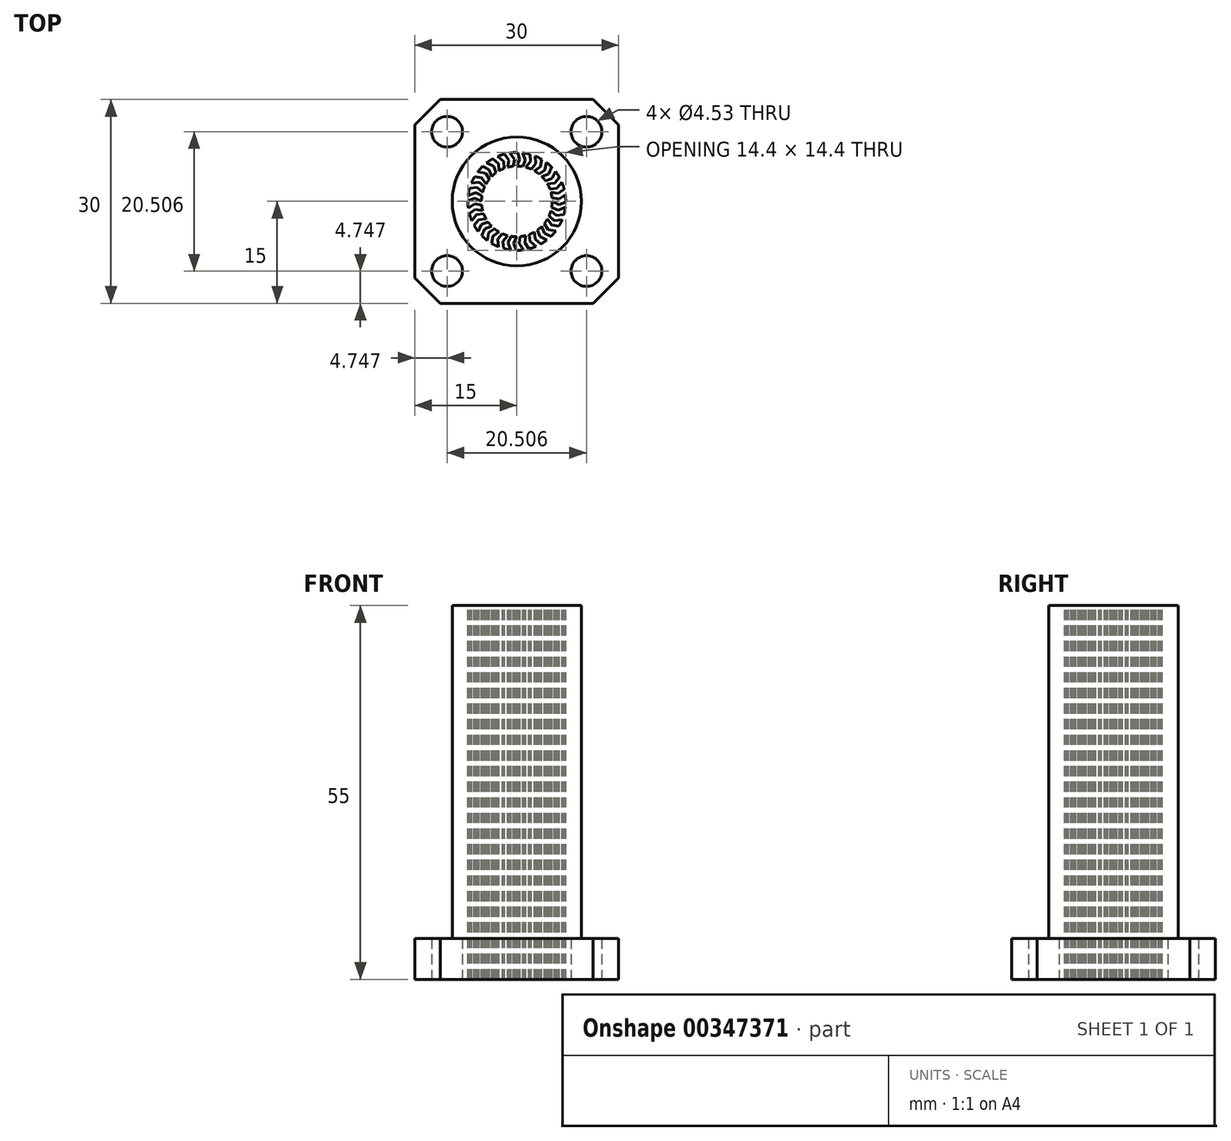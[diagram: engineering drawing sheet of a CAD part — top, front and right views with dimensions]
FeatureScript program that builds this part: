
annotation { "Feature Type Name" : "Feature", "Feature Type Description" : "" }
export const myFeature = defineFeature(function(context is Context, id is Id, definition is map)
    precondition{}
    {
        {
            var Q0;
            Q0=qCreatedBy(makeId("Top.planeOp"),FACE);
            var sketch = newSketch(context, id + "F0", { "sketchPlane" : qUnion([Q0])});
            skLineSegment(sketch, "E0.bottom", {"start": v(15, -15) * mm, "end": v(-15, -15) * mm});
            skLineSegment(sketch, "E0.top", {"start": v(15, 15) * mm, "end": v(-15, 15) * mm});
            skLineSegment(sketch, "E0.left", {"start": v(15, -15) * mm, "end": v(15, 15) * mm});
            skLineSegment(sketch, "E0.right", {"start": v(-15, -15) * mm, "end": v(-15, 15) * mm});
            skPoint(sketch, "E0.middle", {"position": v(0, 0) * mm});
            skSolve(sketch);
        }
        {
            var Q0;
            Q0=makeQuery(id+"F0.imprint","IMPRINT",FACE,{"disambiguationData":[TD([[makeQuery(id+"F0.imprint","IMPRINT",EDGE,{"derivedFrom":sQuery(id+"F0.wireOp",EDGE,"E0.bottom")}),-1.0]])]});
            extrude(context, id + "F1", {"entities" : qUnion([Q0]), "depth" : 6 * mm});
        }
        {
            var Q0;
            Q0=makeQuery(id+"F1.opExtrude","SWEPT_EDGE",EDGE,{"disambiguationData":[OSD([sQuery(id+"F0.wireOp",EDGE,"E0.bottom"),sQuery(id+"F0.wireOp",EDGE,"E0.right")])]});
            var Q1;
            Q1=makeQuery(id+"F1.opExtrude","SWEPT_EDGE",EDGE,{"disambiguationData":[OSD([sQuery(id+"F0.wireOp",EDGE,"E0.top"),sQuery(id+"F0.wireOp",EDGE,"E0.right")])]});
            var Q2;
            Q2=makeQuery(id+"F1.opExtrude","SWEPT_EDGE",EDGE,{"disambiguationData":[OSD([sQuery(id+"F0.wireOp",EDGE,"E0.bottom"),sQuery(id+"F0.wireOp",EDGE,"E0.left")])]});
            var Q3;
            Q3=makeQuery(id+"F1.opExtrude","SWEPT_EDGE",EDGE,{"disambiguationData":[OSD([sQuery(id+"F0.wireOp",EDGE,"E0.top"),sQuery(id+"F0.wireOp",EDGE,"E0.left")])]});
            chamfer(context, id + "F2", {"entities" : qUnion([Q0, Q1, Q2, Q3]), "width" : (7.5 / 2) * mm, "tangentPropagation" : true});
        }
        {
            var Q0;
            Q0=makeQuery(id+"F1.opExtrude","CAP_FACE",FACE,{"disambiguationData":[OSD([sQuery(id+"F0.wireOp",EDGE,"E0.bottom"),sQuery(id+"F0.wireOp",EDGE,"E0.top"),sQuery(id+"F0.wireOp",EDGE,"E0.left"),sQuery(id+"F0.wireOp",EDGE,"E0.right")])],"isStart":true});
            var sketch = newSketch(context, id + "F3", { "sketchPlane" : qUnion([Q0])});
            skCircle(sketch, "E1", {"center": v(0, 0) * mm, "radius": 14.5 * mm});
            skLineSegment(sketch, "E2", {"start": v(-13.13, 13.13) * mm, "end": v(13.13, -13.13) * mm});
            skLineSegment(sketch, "E3", {"start": v(-13.13, -13.12) * mm, "end": v(13.12, 13.12) * mm});
            skPoint(sketch, "E4", {"position": v(-10.25, 10.25) * mm});
            skPoint(sketch, "E5", {"position": v(10.25, 10.25) * mm});
            skPoint(sketch, "E6", {"position": v(10.25, -10.25) * mm});
            skPoint(sketch, "E7", {"position": v(-10.25, -10.25) * mm});
            skSolve(sketch);
        }
        {
            var Q0;
            Q0=sQuery(id+"F3.wireOp",VERTEX,"E4");
            var Q1;
            Q1=sQuery(id+"F3.wireOp",VERTEX,"E5");
            var Q2;
            Q2=sQuery(id+"F3.wireOp",VERTEX,"E7");
            var Q3;
            Q3=sQuery(id+"F3.wireOp",VERTEX,"E6");
            var Q4;
            Q4=makeQuery(id+"F1.opExtrude","SWEPT_BODY",BODY,{"disambiguationData":[OSD([sQuery(id+"F0.wireOp",EDGE,"E0.bottom"),sQuery(id+"F0.wireOp",EDGE,"E0.top"),sQuery(id+"F0.wireOp",EDGE,"E0.left"),sQuery(id+"F0.wireOp",EDGE,"E0.right")])]});
            hole(context, id + "F4", {"style" : HoleStyle.SIMPLE, "endStyle" : HoleEndStyle.THROUGH, "holeDiameter" : 4.53 * mm, "isTappedThrough" : true, "tappedDepth" : 12 * mm, "tapClearance" : 3, "locations" : qUnion([Q0, Q1, Q2, Q3]), "scope" : qUnion([Q4])});
        }
        {
            var Q0;
            Q0=makeQuery(id+"F1.opExtrude","CAP_FACE",FACE,{"disambiguationData":[OSD([sQuery(id+"F0.wireOp",EDGE,"E0.bottom"),sQuery(id+"F0.wireOp",EDGE,"E0.top"),sQuery(id+"F0.wireOp",EDGE,"E0.left"),sQuery(id+"F0.wireOp",EDGE,"E0.right")])],"isStart":false});
            var sketch = newSketch(context, id + "F5", { "sketchPlane" : qUnion([Q0])});
            skCircle(sketch, "E8", {"center": v(0, 0) * mm, "radius": 9.5 * mm});
            skSolve(sketch);
        }
        {
            var Q0;
            Q0=makeQuery(id+"F5.imprint","IMPRINT",FACE,{"disambiguationData":[TD([[makeQuery(id+"F5.imprint","IMPRINT",EDGE,{"derivedFrom":sQuery(id+"F5.wireOp",EDGE,"E8")}),1.0]])]});
            extrude(context, id + "F6", {"entities" : qUnion([Q0]), "operationType" : NewBodyOperationType.ADD, "depth" : 49 * mm});
        }
        {
            var Q0;
            Q0=makeQuery(id+"F6.opExtrude","CAP_FACE",FACE,{"disambiguationData":[OSD([sQuery(id+"F5.wireOp",EDGE,"E8")])],"isStart":false});
            var sketch = newSketch(context, id + "F7", { "sketchPlane" : qUnion([Q0])});
            skCircle(sketch, "E9", {"center": v(0, 0) * mm, "radius": 5.2 * mm});
            skSolve(sketch);
        }
        {
            var Q0;
            Q0=makeQuery(id+"F7.imprint","IMPRINT",FACE,{"disambiguationData":[TD([[makeQuery(id+"F7.imprint","IMPRINT",EDGE,{"derivedFrom":sQuery(id+"F7.wireOp",EDGE,"E9")}),1.0]])]});
            extrude(context, id + "F8", {"entities" : qUnion([Q0]), "operationType" : NewBodyOperationType.REMOVE, "endBound" : BoundingType.UP_TO_NEXT, "oppositeDirection" : true, "depth" : 25 * mm});
        }
        {
            var Q0;
            Q0=makeQuery(id+"F6.opExtrude","CAP_FACE",FACE,{"disambiguationData":[OSD([sQuery(id+"F5.wireOp",EDGE,"E8")])],"isStart":false});
            var sketch = newSketch(context, id + "F9", { "sketchPlane" : qUnion([Q0])});
            skCircle(sketch, "E10.cCircle", {"center": v(0, 5.2) * mm, "radius": 0.5 * mm, "construction": true});
            skLineSegment(sketch, "E10.0", {"start": v(0.29, 4.7) * mm, "end": v(-0.29, 4.7) * mm});
            skLineSegment(sketch, "E10.1", {"start": v(-0.29, 4.7) * mm, "end": v(-0.58, 5.2) * mm});
            skLineSegment(sketch, "E10.2", {"start": v(-0.58, 5.2) * mm, "end": v(-0.29, 5.7) * mm});
            skLineSegment(sketch, "E10.3", {"start": v(-0.29, 5.7) * mm, "end": v(0.29, 5.7) * mm});
            skLineSegment(sketch, "E10.4", {"start": v(0.29, 5.7) * mm, "end": v(0.58, 5.2) * mm});
            skLineSegment(sketch, "E10.5", {"start": v(0.58, 5.2) * mm, "end": v(0.29, 4.7) * mm});
            skPoint(sketch, "E10.0.midPoint", {"position": v(0, 4.7) * mm});
            skLineSegment(sketch, "E11.1.0", {"start": v(-1.91, 5.38) * mm, "end": v(-1.46, 5.03) * mm});
            skPoint(sketch, "E11.1.1", {"position": v(-1.8, 4.34) * mm});
            skCircle(sketch, "E11.1.2", {"center": v(-1.99, 4.8) * mm, "radius": 0.5 * mm, "construction": true});
            skLineSegment(sketch, "E11.1.3", {"start": v(-1.53, 4.45) * mm, "end": v(-2.07, 4.23) * mm});
            skLineSegment(sketch, "E11.1.4", {"start": v(-2.07, 4.23) * mm, "end": v(-2.52, 4.58) * mm});
            skLineSegment(sketch, "E11.1.5", {"start": v(-2.52, 4.58) * mm, "end": v(-2.45, 5.16) * mm});
            skLineSegment(sketch, "E11.1.6", {"start": v(-2.45, 5.16) * mm, "end": v(-1.91, 5.38) * mm});
            skLineSegment(sketch, "E11.1.7", {"start": v(-1.46, 5.03) * mm, "end": v(-1.53, 4.45) * mm});
            skLineSegment(sketch, "E11.2.0", {"start": v(-3.83, 4.23) * mm, "end": v(-3.27, 4.09) * mm});
            skPoint(sketch, "E11.2.1", {"position": v(-3.32, 3.32) * mm});
            skCircle(sketch, "E11.2.2", {"center": v(-3.68, 3.68) * mm, "radius": 0.5 * mm, "construction": true});
            skLineSegment(sketch, "E11.2.3", {"start": v(-3.12, 3.53) * mm, "end": v(-3.53, 3.12) * mm});
            skLineSegment(sketch, "E11.2.4", {"start": v(-3.53, 3.12) * mm, "end": v(-4.09, 3.27) * mm});
            skLineSegment(sketch, "E11.2.5", {"start": v(-4.09, 3.27) * mm, "end": v(-4.23, 3.83) * mm});
            skLineSegment(sketch, "E11.2.6", {"start": v(-4.23, 3.83) * mm, "end": v(-3.83, 4.23) * mm});
            skLineSegment(sketch, "E11.2.7", {"start": v(-3.27, 4.09) * mm, "end": v(-3.12, 3.53) * mm});
            skLineSegment(sketch, "E11.3.0", {"start": v(-5.16, 2.45) * mm, "end": v(-4.58, 2.52) * mm});
            skPoint(sketch, "E11.3.1", {"position": v(-4.34, 1.8) * mm});
            skCircle(sketch, "E11.3.2", {"center": v(-4.8, 1.99) * mm, "radius": 0.5 * mm, "construction": true});
            skLineSegment(sketch, "E11.3.3", {"start": v(-4.23, 2.07) * mm, "end": v(-4.45, 1.53) * mm});
            skLineSegment(sketch, "E11.3.4", {"start": v(-4.45, 1.53) * mm, "end": v(-5.03, 1.46) * mm});
            skLineSegment(sketch, "E11.3.5", {"start": v(-5.03, 1.46) * mm, "end": v(-5.38, 1.91) * mm});
            skLineSegment(sketch, "E11.3.6", {"start": v(-5.38, 1.91) * mm, "end": v(-5.16, 2.45) * mm});
            skLineSegment(sketch, "E11.3.7", {"start": v(-4.58, 2.52) * mm, "end": v(-4.23, 2.07) * mm});
            skLineSegment(sketch, "E11.4.0", {"start": v(-5.7, 0.29) * mm, "end": v(-5.2, 0.58) * mm});
            skPoint(sketch, "E11.4.1", {"position": v(-4.7, 0) * mm});
            skCircle(sketch, "E11.4.2", {"center": v(-5.2, 0) * mm, "radius": 0.5 * mm, "construction": true});
            skLineSegment(sketch, "E11.4.3", {"start": v(-4.7, 0.29) * mm, "end": v(-4.7, -0.29) * mm});
            skLineSegment(sketch, "E11.4.4", {"start": v(-4.7, -0.29) * mm, "end": v(-5.2, -0.58) * mm});
            skLineSegment(sketch, "E11.4.5", {"start": v(-5.2, -0.58) * mm, "end": v(-5.7, -0.29) * mm});
            skLineSegment(sketch, "E11.4.6", {"start": v(-5.7, -0.29) * mm, "end": v(-5.7, 0.29) * mm});
            skLineSegment(sketch, "E11.4.7", {"start": v(-5.2, 0.58) * mm, "end": v(-4.7, 0.29) * mm});
            skLineSegment(sketch, "E11.5.0", {"start": v(-5.38, -1.91) * mm, "end": v(-5.03, -1.46) * mm});
            skPoint(sketch, "E11.5.1", {"position": v(-4.34, -1.8) * mm});
            skCircle(sketch, "E11.5.2", {"center": v(-4.8, -1.99) * mm, "radius": 0.5 * mm, "construction": true});
            skLineSegment(sketch, "E11.5.3", {"start": v(-4.45, -1.53) * mm, "end": v(-4.23, -2.07) * mm});
            skLineSegment(sketch, "E11.5.4", {"start": v(-4.23, -2.07) * mm, "end": v(-4.58, -2.52) * mm});
            skLineSegment(sketch, "E11.5.5", {"start": v(-4.58, -2.52) * mm, "end": v(-5.16, -2.45) * mm});
            skLineSegment(sketch, "E11.5.6", {"start": v(-5.16, -2.45) * mm, "end": v(-5.38, -1.91) * mm});
            skLineSegment(sketch, "E11.5.7", {"start": v(-5.03, -1.46) * mm, "end": v(-4.45, -1.53) * mm});
            skLineSegment(sketch, "E11.6.0", {"start": v(-4.23, -3.83) * mm, "end": v(-4.09, -3.27) * mm});
            skPoint(sketch, "E11.6.1", {"position": v(-3.32, -3.32) * mm});
            skCircle(sketch, "E11.6.2", {"center": v(-3.68, -3.68) * mm, "radius": 0.5 * mm, "construction": true});
            skLineSegment(sketch, "E11.6.3", {"start": v(-3.53, -3.12) * mm, "end": v(-3.12, -3.53) * mm});
            skLineSegment(sketch, "E11.6.4", {"start": v(-3.12, -3.53) * mm, "end": v(-3.27, -4.09) * mm});
            skLineSegment(sketch, "E11.6.5", {"start": v(-3.27, -4.09) * mm, "end": v(-3.83, -4.23) * mm});
            skLineSegment(sketch, "E11.6.6", {"start": v(-3.83, -4.23) * mm, "end": v(-4.23, -3.83) * mm});
            skLineSegment(sketch, "E11.6.7", {"start": v(-4.09, -3.27) * mm, "end": v(-3.53, -3.12) * mm});
            skLineSegment(sketch, "E11.7.0", {"start": v(-2.45, -5.16) * mm, "end": v(-2.52, -4.58) * mm});
            skPoint(sketch, "E11.7.1", {"position": v(-1.8, -4.34) * mm});
            skCircle(sketch, "E11.7.2", {"center": v(-1.99, -4.8) * mm, "radius": 0.5 * mm, "construction": true});
            skLineSegment(sketch, "E11.7.3", {"start": v(-2.07, -4.23) * mm, "end": v(-1.53, -4.45) * mm});
            skLineSegment(sketch, "E11.7.4", {"start": v(-1.53, -4.45) * mm, "end": v(-1.46, -5.03) * mm});
            skLineSegment(sketch, "E11.7.5", {"start": v(-1.46, -5.03) * mm, "end": v(-1.91, -5.38) * mm});
            skLineSegment(sketch, "E11.7.6", {"start": v(-1.91, -5.38) * mm, "end": v(-2.45, -5.16) * mm});
            skLineSegment(sketch, "E11.7.7", {"start": v(-2.52, -4.58) * mm, "end": v(-2.07, -4.23) * mm});
            skLineSegment(sketch, "E11.8.0", {"start": v(-0.29, -5.7) * mm, "end": v(-0.58, -5.2) * mm});
            skPoint(sketch, "E11.8.1", {"position": v(0, -4.7) * mm});
            skCircle(sketch, "E11.8.2", {"center": v(0, -5.2) * mm, "radius": 0.5 * mm, "construction": true});
            skLineSegment(sketch, "E11.8.3", {"start": v(-0.29, -4.7) * mm, "end": v(0.29, -4.7) * mm});
            skLineSegment(sketch, "E11.8.4", {"start": v(0.29, -4.7) * mm, "end": v(0.58, -5.2) * mm});
            skLineSegment(sketch, "E11.8.5", {"start": v(0.58, -5.2) * mm, "end": v(0.29, -5.7) * mm});
            skLineSegment(sketch, "E11.8.6", {"start": v(0.29, -5.7) * mm, "end": v(-0.29, -5.7) * mm});
            skLineSegment(sketch, "E11.8.7", {"start": v(-0.58, -5.2) * mm, "end": v(-0.29, -4.7) * mm});
            skLineSegment(sketch, "E11.9.0", {"start": v(1.91, -5.38) * mm, "end": v(1.46, -5.03) * mm});
            skPoint(sketch, "E11.9.1", {"position": v(1.8, -4.34) * mm});
            skCircle(sketch, "E11.9.2", {"center": v(1.99, -4.8) * mm, "radius": 0.5 * mm, "construction": true});
            skLineSegment(sketch, "E11.9.3", {"start": v(1.53, -4.45) * mm, "end": v(2.07, -4.23) * mm});
            skLineSegment(sketch, "E11.9.4", {"start": v(2.07, -4.23) * mm, "end": v(2.52, -4.58) * mm});
            skLineSegment(sketch, "E11.9.5", {"start": v(2.52, -4.58) * mm, "end": v(2.45, -5.16) * mm});
            skLineSegment(sketch, "E11.9.6", {"start": v(2.45, -5.16) * mm, "end": v(1.91, -5.38) * mm});
            skLineSegment(sketch, "E11.9.7", {"start": v(1.46, -5.03) * mm, "end": v(1.53, -4.45) * mm});
            skLineSegment(sketch, "E11.10.0", {"start": v(3.83, -4.23) * mm, "end": v(3.27, -4.09) * mm});
            skPoint(sketch, "E11.10.1", {"position": v(3.32, -3.32) * mm});
            skCircle(sketch, "E11.10.2", {"center": v(3.68, -3.68) * mm, "radius": 0.5 * mm, "construction": true});
            skLineSegment(sketch, "E11.10.3", {"start": v(3.12, -3.53) * mm, "end": v(3.53, -3.12) * mm});
            skLineSegment(sketch, "E11.10.4", {"start": v(3.53, -3.12) * mm, "end": v(4.09, -3.27) * mm});
            skLineSegment(sketch, "E11.10.5", {"start": v(4.09, -3.27) * mm, "end": v(4.23, -3.83) * mm});
            skLineSegment(sketch, "E11.10.6", {"start": v(4.23, -3.83) * mm, "end": v(3.83, -4.23) * mm});
            skLineSegment(sketch, "E11.10.7", {"start": v(3.27, -4.09) * mm, "end": v(3.12, -3.53) * mm});
            skLineSegment(sketch, "E11.11.0", {"start": v(5.16, -2.45) * mm, "end": v(4.58, -2.52) * mm});
            skPoint(sketch, "E11.11.1", {"position": v(4.34, -1.8) * mm});
            skCircle(sketch, "E11.11.2", {"center": v(4.8, -1.99) * mm, "radius": 0.5 * mm, "construction": true});
            skLineSegment(sketch, "E11.11.3", {"start": v(4.23, -2.07) * mm, "end": v(4.45, -1.53) * mm});
            skLineSegment(sketch, "E11.11.4", {"start": v(4.45, -1.53) * mm, "end": v(5.03, -1.46) * mm});
            skLineSegment(sketch, "E11.11.5", {"start": v(5.03, -1.46) * mm, "end": v(5.38, -1.91) * mm});
            skLineSegment(sketch, "E11.11.6", {"start": v(5.38, -1.91) * mm, "end": v(5.16, -2.45) * mm});
            skLineSegment(sketch, "E11.11.7", {"start": v(4.58, -2.52) * mm, "end": v(4.23, -2.07) * mm});
            skLineSegment(sketch, "E11.12.0", {"start": v(5.7, -0.29) * mm, "end": v(5.2, -0.58) * mm});
            skPoint(sketch, "E11.12.1", {"position": v(4.7, 0) * mm});
            skCircle(sketch, "E11.12.2", {"center": v(5.2, 0) * mm, "radius": 0.5 * mm, "construction": true});
            skLineSegment(sketch, "E11.12.3", {"start": v(4.7, -0.29) * mm, "end": v(4.7, 0.29) * mm});
            skLineSegment(sketch, "E11.12.4", {"start": v(4.7, 0.29) * mm, "end": v(5.2, 0.58) * mm});
            skLineSegment(sketch, "E11.12.5", {"start": v(5.2, 0.58) * mm, "end": v(5.7, 0.29) * mm});
            skLineSegment(sketch, "E11.12.6", {"start": v(5.7, 0.29) * mm, "end": v(5.7, -0.29) * mm});
            skLineSegment(sketch, "E11.12.7", {"start": v(5.2, -0.58) * mm, "end": v(4.7, -0.29) * mm});
            skLineSegment(sketch, "E11.13.0", {"start": v(5.38, 1.91) * mm, "end": v(5.03, 1.46) * mm});
            skPoint(sketch, "E11.13.1", {"position": v(4.34, 1.8) * mm});
            skCircle(sketch, "E11.13.2", {"center": v(4.8, 1.99) * mm, "radius": 0.5 * mm, "construction": true});
            skLineSegment(sketch, "E11.13.3", {"start": v(4.45, 1.53) * mm, "end": v(4.23, 2.07) * mm});
            skLineSegment(sketch, "E11.13.4", {"start": v(4.23, 2.07) * mm, "end": v(4.58, 2.52) * mm});
            skLineSegment(sketch, "E11.13.5", {"start": v(4.58, 2.52) * mm, "end": v(5.16, 2.45) * mm});
            skLineSegment(sketch, "E11.13.6", {"start": v(5.16, 2.45) * mm, "end": v(5.38, 1.91) * mm});
            skLineSegment(sketch, "E11.13.7", {"start": v(5.03, 1.46) * mm, "end": v(4.45, 1.53) * mm});
            skLineSegment(sketch, "E11.14.0", {"start": v(4.23, 3.83) * mm, "end": v(4.09, 3.27) * mm});
            skPoint(sketch, "E11.14.1", {"position": v(3.32, 3.32) * mm});
            skCircle(sketch, "E11.14.2", {"center": v(3.68, 3.68) * mm, "radius": 0.5 * mm, "construction": true});
            skLineSegment(sketch, "E11.14.3", {"start": v(3.53, 3.12) * mm, "end": v(3.12, 3.53) * mm});
            skLineSegment(sketch, "E11.14.4", {"start": v(3.12, 3.53) * mm, "end": v(3.27, 4.09) * mm});
            skLineSegment(sketch, "E11.14.5", {"start": v(3.27, 4.09) * mm, "end": v(3.83, 4.23) * mm});
            skLineSegment(sketch, "E11.14.6", {"start": v(3.83, 4.23) * mm, "end": v(4.23, 3.83) * mm});
            skLineSegment(sketch, "E11.14.7", {"start": v(4.09, 3.27) * mm, "end": v(3.53, 3.12) * mm});
            skLineSegment(sketch, "E11.15.0", {"start": v(2.45, 5.16) * mm, "end": v(2.52, 4.58) * mm});
            skPoint(sketch, "E11.15.1", {"position": v(1.8, 4.34) * mm});
            skCircle(sketch, "E11.15.2", {"center": v(1.99, 4.8) * mm, "radius": 0.5 * mm, "construction": true});
            skLineSegment(sketch, "E11.15.3", {"start": v(2.07, 4.23) * mm, "end": v(1.53, 4.45) * mm});
            skLineSegment(sketch, "E11.15.4", {"start": v(1.53, 4.45) * mm, "end": v(1.46, 5.03) * mm});
            skLineSegment(sketch, "E11.15.5", {"start": v(1.46, 5.03) * mm, "end": v(1.91, 5.38) * mm});
            skLineSegment(sketch, "E11.15.6", {"start": v(1.91, 5.38) * mm, "end": v(2.45, 5.16) * mm});
            skLineSegment(sketch, "E11.15.7", {"start": v(2.52, 4.58) * mm, "end": v(2.07, 4.23) * mm});
            skPoint(sketch, "E11.center", {"position": v(0, 0) * mm});
            skSolve(sketch);
        }
        {
            var Q0;
            Q0=makeQuery(id+"F6.opExtrude","CAP_FACE",FACE,{"disambiguationData":[OSD([sQuery(id+"F5.wireOp",EDGE,"E8")])],"isStart":false});
            var sketch = newSketch(context, id + "F10", { "sketchPlane" : qUnion([Q0])});
            skLineSegment(sketch, "E12.bottom", {"start": v(0.5, 3.7) * mm, "end": v(-0.5, 3.7) * mm});
            skLineSegment(sketch, "E12.top", {"start": v(0.5, 6.7) * mm, "end": v(-0.5, 6.7) * mm});
            skLineSegment(sketch, "E12.left", {"start": v(0.5, 3.7) * mm, "end": v(0.5, 6.7) * mm});
            skLineSegment(sketch, "E12.right", {"start": v(-0.5, 3.7) * mm, "end": v(-0.5, 6.7) * mm});
            skPoint(sketch, "E12.middle", {"position": v(0, 5.2) * mm});
            skLineSegment(sketch, "E13.1.0", {"start": v(-0.95, 3.6) * mm, "end": v(-2.1, 6.38) * mm});
            skLineSegment(sketch, "E13.1.1", {"start": v(-2.1, 6.38) * mm, "end": v(-3.03, 6) * mm});
            skLineSegment(sketch, "E13.1.2", {"start": v(-0.95, 3.6) * mm, "end": v(-1.88, 3.23) * mm});
            skPoint(sketch, "E13.1.3", {"position": v(-1.99, 4.8) * mm});
            skLineSegment(sketch, "E13.1.4", {"start": v(-1.88, 3.23) * mm, "end": v(-3.03, 6) * mm});
            skLineSegment(sketch, "E13.2.0", {"start": v(-2.26, 2.97) * mm, "end": v(-4.38, 5.1) * mm});
            skLineSegment(sketch, "E13.2.1", {"start": v(-4.38, 5.1) * mm, "end": v(-5.1, 4.38) * mm});
            skLineSegment(sketch, "E13.2.2", {"start": v(-2.26, 2.97) * mm, "end": v(-2.97, 2.26) * mm});
            skPoint(sketch, "E13.2.3", {"position": v(-3.68, 3.68) * mm});
            skLineSegment(sketch, "E13.2.4", {"start": v(-2.97, 2.26) * mm, "end": v(-5.1, 4.38) * mm});
            skLineSegment(sketch, "E13.3.0", {"start": v(-3.23, 1.88) * mm, "end": v(-6, 3.03) * mm});
            skLineSegment(sketch, "E13.3.1", {"start": v(-6, 3.03) * mm, "end": v(-6.38, 2.1) * mm});
            skLineSegment(sketch, "E13.3.2", {"start": v(-3.23, 1.88) * mm, "end": v(-3.6, 0.95) * mm});
            skPoint(sketch, "E13.3.3", {"position": v(-4.8, 1.99) * mm});
            skLineSegment(sketch, "E13.3.4", {"start": v(-3.6, 0.95) * mm, "end": v(-6.38, 2.1) * mm});
            skLineSegment(sketch, "E13.4.0", {"start": v(-3.7, 0.5) * mm, "end": v(-6.7, 0.5) * mm});
            skLineSegment(sketch, "E13.4.1", {"start": v(-6.7, 0.5) * mm, "end": v(-6.7, -0.5) * mm});
            skLineSegment(sketch, "E13.4.2", {"start": v(-3.7, 0.5) * mm, "end": v(-3.7, -0.5) * mm});
            skPoint(sketch, "E13.4.3", {"position": v(-5.2, 0) * mm});
            skLineSegment(sketch, "E13.4.4", {"start": v(-3.7, -0.5) * mm, "end": v(-6.7, -0.5) * mm});
            skLineSegment(sketch, "E13.5.0", {"start": v(-3.6, -0.95) * mm, "end": v(-6.38, -2.1) * mm});
            skLineSegment(sketch, "E13.5.1", {"start": v(-6.38, -2.1) * mm, "end": v(-6, -3.03) * mm});
            skLineSegment(sketch, "E13.5.2", {"start": v(-3.6, -0.95) * mm, "end": v(-3.23, -1.88) * mm});
            skPoint(sketch, "E13.5.3", {"position": v(-4.8, -1.99) * mm});
            skLineSegment(sketch, "E13.5.4", {"start": v(-3.23, -1.88) * mm, "end": v(-6, -3.03) * mm});
            skLineSegment(sketch, "E13.6.0", {"start": v(-2.97, -2.26) * mm, "end": v(-5.1, -4.38) * mm});
            skLineSegment(sketch, "E13.6.1", {"start": v(-5.1, -4.38) * mm, "end": v(-4.38, -5.1) * mm});
            skLineSegment(sketch, "E13.6.2", {"start": v(-2.97, -2.26) * mm, "end": v(-2.26, -2.97) * mm});
            skPoint(sketch, "E13.6.3", {"position": v(-3.68, -3.68) * mm});
            skLineSegment(sketch, "E13.6.4", {"start": v(-2.26, -2.97) * mm, "end": v(-4.38, -5.1) * mm});
            skLineSegment(sketch, "E13.7.0", {"start": v(-1.88, -3.23) * mm, "end": v(-3.03, -6) * mm});
            skLineSegment(sketch, "E13.7.1", {"start": v(-3.03, -6) * mm, "end": v(-2.1, -6.38) * mm});
            skLineSegment(sketch, "E13.7.2", {"start": v(-1.88, -3.23) * mm, "end": v(-0.95, -3.6) * mm});
            skPoint(sketch, "E13.7.3", {"position": v(-1.99, -4.8) * mm});
            skLineSegment(sketch, "E13.7.4", {"start": v(-0.95, -3.6) * mm, "end": v(-2.1, -6.38) * mm});
            skLineSegment(sketch, "E13.8.0", {"start": v(-0.5, -3.7) * mm, "end": v(-0.5, -6.7) * mm});
            skLineSegment(sketch, "E13.8.1", {"start": v(-0.5, -6.7) * mm, "end": v(0.5, -6.7) * mm});
            skLineSegment(sketch, "E13.8.2", {"start": v(-0.5, -3.7) * mm, "end": v(0.5, -3.7) * mm});
            skPoint(sketch, "E13.8.3", {"position": v(0, -5.2) * mm});
            skLineSegment(sketch, "E13.8.4", {"start": v(0.5, -3.7) * mm, "end": v(0.5, -6.7) * mm});
            skLineSegment(sketch, "E13.9.0", {"start": v(0.95, -3.6) * mm, "end": v(2.1, -6.38) * mm});
            skLineSegment(sketch, "E13.9.1", {"start": v(2.1, -6.38) * mm, "end": v(3.03, -6) * mm});
            skLineSegment(sketch, "E13.9.2", {"start": v(0.95, -3.6) * mm, "end": v(1.88, -3.23) * mm});
            skPoint(sketch, "E13.9.3", {"position": v(1.99, -4.8) * mm});
            skLineSegment(sketch, "E13.9.4", {"start": v(1.88, -3.23) * mm, "end": v(3.03, -6) * mm});
            skLineSegment(sketch, "E13.10.0", {"start": v(2.26, -2.97) * mm, "end": v(4.38, -5.1) * mm});
            skLineSegment(sketch, "E13.10.1", {"start": v(4.38, -5.1) * mm, "end": v(5.1, -4.38) * mm});
            skLineSegment(sketch, "E13.10.2", {"start": v(2.26, -2.97) * mm, "end": v(2.97, -2.26) * mm});
            skPoint(sketch, "E13.10.3", {"position": v(3.68, -3.68) * mm});
            skLineSegment(sketch, "E13.10.4", {"start": v(2.97, -2.26) * mm, "end": v(5.1, -4.38) * mm});
            skLineSegment(sketch, "E13.11.0", {"start": v(3.23, -1.88) * mm, "end": v(6, -3.03) * mm});
            skLineSegment(sketch, "E13.11.1", {"start": v(6, -3.03) * mm, "end": v(6.38, -2.1) * mm});
            skLineSegment(sketch, "E13.11.2", {"start": v(3.23, -1.88) * mm, "end": v(3.6, -0.95) * mm});
            skPoint(sketch, "E13.11.3", {"position": v(4.8, -1.99) * mm});
            skLineSegment(sketch, "E13.11.4", {"start": v(3.6, -0.95) * mm, "end": v(6.38, -2.1) * mm});
            skLineSegment(sketch, "E13.12.0", {"start": v(3.7, -0.5) * mm, "end": v(6.7, -0.5) * mm});
            skLineSegment(sketch, "E13.12.1", {"start": v(6.7, -0.5) * mm, "end": v(6.7, 0.5) * mm});
            skLineSegment(sketch, "E13.12.2", {"start": v(3.7, -0.5) * mm, "end": v(3.7, 0.5) * mm});
            skPoint(sketch, "E13.12.3", {"position": v(5.2, 0) * mm});
            skLineSegment(sketch, "E13.12.4", {"start": v(3.7, 0.5) * mm, "end": v(6.7, 0.5) * mm});
            skLineSegment(sketch, "E13.13.0", {"start": v(3.6, 0.95) * mm, "end": v(6.38, 2.1) * mm});
            skLineSegment(sketch, "E13.13.1", {"start": v(6.38, 2.1) * mm, "end": v(6, 3.03) * mm});
            skLineSegment(sketch, "E13.13.2", {"start": v(3.6, 0.95) * mm, "end": v(3.23, 1.88) * mm});
            skPoint(sketch, "E13.13.3", {"position": v(4.8, 1.99) * mm});
            skLineSegment(sketch, "E13.13.4", {"start": v(3.23, 1.88) * mm, "end": v(6, 3.03) * mm});
            skLineSegment(sketch, "E13.14.0", {"start": v(2.97, 2.26) * mm, "end": v(5.1, 4.38) * mm});
            skLineSegment(sketch, "E13.14.1", {"start": v(5.1, 4.38) * mm, "end": v(4.38, 5.1) * mm});
            skLineSegment(sketch, "E13.14.2", {"start": v(2.97, 2.26) * mm, "end": v(2.26, 2.97) * mm});
            skPoint(sketch, "E13.14.3", {"position": v(3.68, 3.68) * mm});
            skLineSegment(sketch, "E13.14.4", {"start": v(2.26, 2.97) * mm, "end": v(4.38, 5.1) * mm});
            skLineSegment(sketch, "E13.15.0", {"start": v(1.88, 3.23) * mm, "end": v(3.03, 6) * mm});
            skLineSegment(sketch, "E13.15.1", {"start": v(3.03, 6) * mm, "end": v(2.1, 6.38) * mm});
            skLineSegment(sketch, "E13.15.2", {"start": v(1.88, 3.23) * mm, "end": v(0.95, 3.6) * mm});
            skPoint(sketch, "E13.15.3", {"position": v(1.99, 4.8) * mm});
            skLineSegment(sketch, "E13.15.4", {"start": v(0.95, 3.6) * mm, "end": v(2.1, 6.38) * mm});
            skPoint(sketch, "E13.center", {"position": v(0, 0) * mm});
            skSolve(sketch);
        }
        {
            var Q0;
            Q0=makeQuery(id+"F6.opExtrude","CAP_FACE",FACE,{"disambiguationData":[OSD([sQuery(id+"F5.wireOp",EDGE,"E8")])],"isStart":false});
            var sketch = newSketch(context, id + "F11", { "sketchPlane" : qUnion([Q0])});
            skCircle(sketch, "E14", {"center": v(0, 0) * mm, "radius": 6.2 * mm});
            skCircle(sketch, "E15", {"center": v(0, 0) * mm, "radius": 7.2 * mm});
            skLineSegment(sketch, "E16", {"start": v(0, 5.2) * mm, "end": v(0.45, 6.18) * mm});
            skLineSegment(sketch, "E17", {"start": v(0.45, 6.18) * mm, "end": v(0.08, 7.2) * mm});
            skLineSegment(sketch, "E18", {"start": v(0.84, 5.13) * mm, "end": v(1.28, 6.07) * mm});
            skLineSegment(sketch, "E19", {"start": v(1.28, 6.07) * mm, "end": v(0.88, 7.15) * mm});
            skLineSegment(sketch, "E20.1.0", {"start": v(-0.34, 6.2) * mm, "end": v(-1, 7.13) * mm});
            skLineSegment(sketch, "E20.1.1", {"start": v(-1.16, 6.1) * mm, "end": v(-1.79, 6.97) * mm});
            skLineSegment(sketch, "E20.1.2", {"start": v(-1.35, 5.02) * mm, "end": v(-1.16, 6.1) * mm});
            skLineSegment(sketch, "E20.1.3", {"start": v(-0.51, 5.17) * mm, "end": v(-0.34, 6.2) * mm});
            skLineSegment(sketch, "E20.2.0", {"start": v(-1.93, 5.9) * mm, "end": v(-2.81, 6.63) * mm});
            skLineSegment(sketch, "E20.2.1", {"start": v(-2.7, 5.58) * mm, "end": v(-3.53, 6.27) * mm});
            skLineSegment(sketch, "E20.2.2", {"start": v(-2.6, 4.5) * mm, "end": v(-2.7, 5.58) * mm});
            skLineSegment(sketch, "E20.2.3", {"start": v(-1.84, 4.87) * mm, "end": v(-1.93, 5.9) * mm});
            skLineSegment(sketch, "E20.3.0", {"start": v(-3.39, 5.2) * mm, "end": v(-4.43, 5.67) * mm});
            skLineSegment(sketch, "E20.3.1", {"start": v(-4.05, 4.7) * mm, "end": v(-5.03, 5.15) * mm});
            skLineSegment(sketch, "E20.3.2", {"start": v(-3.68, 3.68) * mm, "end": v(-4.05, 4.7) * mm});
            skLineSegment(sketch, "E20.3.3", {"start": v(-3.03, 4.22) * mm, "end": v(-3.39, 5.2) * mm});
            skLineSegment(sketch, "E20.4.0", {"start": v(-4.62, 4.14) * mm, "end": v(-5.75, 4.33) * mm});
            skLineSegment(sketch, "E20.4.1", {"start": v(-5.13, 3.48) * mm, "end": v(-6.2, 3.67) * mm});
            skLineSegment(sketch, "E20.4.2", {"start": v(-4.5, 2.6) * mm, "end": v(-5.13, 3.48) * mm});
            skLineSegment(sketch, "E20.4.3", {"start": v(-4.02, 3.3) * mm, "end": v(-4.62, 4.14) * mm});
            skLineSegment(sketch, "E20.5.0", {"start": v(-5.53, 2.8) * mm, "end": v(-6.68, 2.7) * mm});
            skLineSegment(sketch, "E20.5.1", {"start": v(-5.86, 2.04) * mm, "end": v(-6.93, 1.94) * mm});
            skLineSegment(sketch, "E20.5.2", {"start": v(-5.02, 1.35) * mm, "end": v(-5.86, 2.04) * mm});
            skLineSegment(sketch, "E20.5.3", {"start": v(-4.74, 2.14) * mm, "end": v(-5.53, 2.8) * mm});
            skLineSegment(sketch, "E20.6.0", {"start": v(-6.07, 1.28) * mm, "end": v(-7.15, 0.88) * mm});
            skLineSegment(sketch, "E20.6.1", {"start": v(-6.18, 0.45) * mm, "end": v(-7.2, 0.08) * mm});
            skLineSegment(sketch, "E20.6.2", {"start": v(-5.2, 0) * mm, "end": v(-6.18, 0.45) * mm});
            skLineSegment(sketch, "E20.6.3", {"start": v(-5.13, 0.84) * mm, "end": v(-6.07, 1.28) * mm});
            skLineSegment(sketch, "E20.7.0", {"start": v(-6.2, -0.34) * mm, "end": v(-7.13, -1) * mm});
            skLineSegment(sketch, "E20.7.1", {"start": v(-6.1, -1.16) * mm, "end": v(-6.97, -1.79) * mm});
            skLineSegment(sketch, "E20.7.2", {"start": v(-5.02, -1.35) * mm, "end": v(-6.1, -1.16) * mm});
            skLineSegment(sketch, "E20.7.3", {"start": v(-5.17, -0.51) * mm, "end": v(-6.2, -0.34) * mm});
            skLineSegment(sketch, "E20.8.0", {"start": v(-5.9, -1.93) * mm, "end": v(-6.63, -2.81) * mm});
            skLineSegment(sketch, "E20.8.1", {"start": v(-5.58, -2.7) * mm, "end": v(-6.27, -3.53) * mm});
            skLineSegment(sketch, "E20.8.2", {"start": v(-4.5, -2.6) * mm, "end": v(-5.58, -2.7) * mm});
            skLineSegment(sketch, "E20.8.3", {"start": v(-4.87, -1.84) * mm, "end": v(-5.9, -1.93) * mm});
            skLineSegment(sketch, "E20.9.0", {"start": v(-5.2, -3.39) * mm, "end": v(-5.67, -4.43) * mm});
            skLineSegment(sketch, "E20.9.1", {"start": v(-4.7, -4.05) * mm, "end": v(-5.15, -5.03) * mm});
            skLineSegment(sketch, "E20.9.2", {"start": v(-3.68, -3.68) * mm, "end": v(-4.7, -4.05) * mm});
            skLineSegment(sketch, "E20.9.3", {"start": v(-4.22, -3.03) * mm, "end": v(-5.2, -3.39) * mm});
            skLineSegment(sketch, "E20.10.0", {"start": v(-4.14, -4.62) * mm, "end": v(-4.33, -5.75) * mm});
            skLineSegment(sketch, "E20.10.1", {"start": v(-3.48, -5.13) * mm, "end": v(-3.67, -6.2) * mm});
            skLineSegment(sketch, "E20.10.2", {"start": v(-2.6, -4.5) * mm, "end": v(-3.48, -5.13) * mm});
            skLineSegment(sketch, "E20.10.3", {"start": v(-3.3, -4.02) * mm, "end": v(-4.14, -4.62) * mm});
            skLineSegment(sketch, "E20.11.0", {"start": v(-2.8, -5.53) * mm, "end": v(-2.7, -6.68) * mm});
            skLineSegment(sketch, "E20.11.1", {"start": v(-2.04, -5.86) * mm, "end": v(-1.94, -6.93) * mm});
            skLineSegment(sketch, "E20.11.2", {"start": v(-1.35, -5.02) * mm, "end": v(-2.04, -5.86) * mm});
            skLineSegment(sketch, "E20.11.3", {"start": v(-2.14, -4.74) * mm, "end": v(-2.8, -5.53) * mm});
            skLineSegment(sketch, "E20.12.0", {"start": v(-1.28, -6.07) * mm, "end": v(-0.88, -7.15) * mm});
            skLineSegment(sketch, "E20.12.1", {"start": v(-0.45, -6.18) * mm, "end": v(-0.08, -7.2) * mm});
            skLineSegment(sketch, "E20.12.2", {"start": v(0, -5.2) * mm, "end": v(-0.45, -6.18) * mm});
            skLineSegment(sketch, "E20.12.3", {"start": v(-0.84, -5.13) * mm, "end": v(-1.28, -6.07) * mm});
            skLineSegment(sketch, "E20.13.0", {"start": v(0.34, -6.2) * mm, "end": v(1, -7.13) * mm});
            skLineSegment(sketch, "E20.13.1", {"start": v(1.16, -6.1) * mm, "end": v(1.79, -6.97) * mm});
            skLineSegment(sketch, "E20.13.2", {"start": v(1.35, -5.02) * mm, "end": v(1.16, -6.1) * mm});
            skLineSegment(sketch, "E20.13.3", {"start": v(0.51, -5.17) * mm, "end": v(0.34, -6.2) * mm});
            skLineSegment(sketch, "E20.14.0", {"start": v(1.93, -5.9) * mm, "end": v(2.81, -6.63) * mm});
            skLineSegment(sketch, "E20.14.1", {"start": v(2.7, -5.58) * mm, "end": v(3.53, -6.27) * mm});
            skLineSegment(sketch, "E20.14.2", {"start": v(2.6, -4.5) * mm, "end": v(2.7, -5.58) * mm});
            skLineSegment(sketch, "E20.14.3", {"start": v(1.84, -4.87) * mm, "end": v(1.93, -5.9) * mm});
            skLineSegment(sketch, "E20.15.0", {"start": v(3.39, -5.2) * mm, "end": v(4.43, -5.67) * mm});
            skLineSegment(sketch, "E20.15.1", {"start": v(4.05, -4.7) * mm, "end": v(5.03, -5.15) * mm});
            skLineSegment(sketch, "E20.15.2", {"start": v(3.68, -3.68) * mm, "end": v(4.05, -4.7) * mm});
            skLineSegment(sketch, "E20.15.3", {"start": v(3.03, -4.22) * mm, "end": v(3.39, -5.2) * mm});
            skLineSegment(sketch, "E20.16.0", {"start": v(4.62, -4.14) * mm, "end": v(5.75, -4.33) * mm});
            skLineSegment(sketch, "E20.16.1", {"start": v(5.13, -3.48) * mm, "end": v(6.2, -3.67) * mm});
            skLineSegment(sketch, "E20.16.2", {"start": v(4.5, -2.6) * mm, "end": v(5.13, -3.48) * mm});
            skLineSegment(sketch, "E20.16.3", {"start": v(4.02, -3.3) * mm, "end": v(4.62, -4.14) * mm});
            skLineSegment(sketch, "E20.17.0", {"start": v(5.53, -2.8) * mm, "end": v(6.68, -2.7) * mm});
            skLineSegment(sketch, "E20.17.1", {"start": v(5.86, -2.04) * mm, "end": v(6.93, -1.94) * mm});
            skLineSegment(sketch, "E20.17.2", {"start": v(5.02, -1.35) * mm, "end": v(5.86, -2.04) * mm});
            skLineSegment(sketch, "E20.17.3", {"start": v(4.74, -2.14) * mm, "end": v(5.53, -2.8) * mm});
            skLineSegment(sketch, "E20.18.0", {"start": v(6.07, -1.28) * mm, "end": v(7.15, -0.88) * mm});
            skLineSegment(sketch, "E20.18.1", {"start": v(6.18, -0.45) * mm, "end": v(7.2, -0.08) * mm});
            skLineSegment(sketch, "E20.18.2", {"start": v(5.2, 0) * mm, "end": v(6.18, -0.45) * mm});
            skLineSegment(sketch, "E20.18.3", {"start": v(5.13, -0.84) * mm, "end": v(6.07, -1.28) * mm});
            skLineSegment(sketch, "E20.19.0", {"start": v(6.2, 0.34) * mm, "end": v(7.13, 1) * mm});
            skLineSegment(sketch, "E20.19.1", {"start": v(6.1, 1.16) * mm, "end": v(6.97, 1.79) * mm});
            skLineSegment(sketch, "E20.19.2", {"start": v(5.02, 1.35) * mm, "end": v(6.1, 1.16) * mm});
            skLineSegment(sketch, "E20.19.3", {"start": v(5.17, 0.51) * mm, "end": v(6.2, 0.34) * mm});
            skLineSegment(sketch, "E20.20.0", {"start": v(5.9, 1.93) * mm, "end": v(6.63, 2.81) * mm});
            skLineSegment(sketch, "E20.20.1", {"start": v(5.58, 2.7) * mm, "end": v(6.27, 3.53) * mm});
            skLineSegment(sketch, "E20.20.2", {"start": v(4.5, 2.6) * mm, "end": v(5.58, 2.7) * mm});
            skLineSegment(sketch, "E20.20.3", {"start": v(4.87, 1.84) * mm, "end": v(5.9, 1.93) * mm});
            skLineSegment(sketch, "E20.21.0", {"start": v(5.2, 3.39) * mm, "end": v(5.67, 4.43) * mm});
            skLineSegment(sketch, "E20.21.1", {"start": v(4.7, 4.05) * mm, "end": v(5.15, 5.03) * mm});
            skLineSegment(sketch, "E20.21.2", {"start": v(3.68, 3.68) * mm, "end": v(4.7, 4.05) * mm});
            skLineSegment(sketch, "E20.21.3", {"start": v(4.22, 3.03) * mm, "end": v(5.2, 3.39) * mm});
            skLineSegment(sketch, "E20.22.0", {"start": v(4.14, 4.62) * mm, "end": v(4.33, 5.75) * mm});
            skLineSegment(sketch, "E20.22.1", {"start": v(3.48, 5.13) * mm, "end": v(3.67, 6.2) * mm});
            skLineSegment(sketch, "E20.22.2", {"start": v(2.6, 4.5) * mm, "end": v(3.48, 5.13) * mm});
            skLineSegment(sketch, "E20.22.3", {"start": v(3.3, 4.02) * mm, "end": v(4.14, 4.62) * mm});
            skLineSegment(sketch, "E20.23.0", {"start": v(2.8, 5.53) * mm, "end": v(2.7, 6.68) * mm});
            skLineSegment(sketch, "E20.23.1", {"start": v(2.04, 5.86) * mm, "end": v(1.94, 6.93) * mm});
            skLineSegment(sketch, "E20.23.2", {"start": v(1.35, 5.02) * mm, "end": v(2.04, 5.86) * mm});
            skLineSegment(sketch, "E20.23.3", {"start": v(2.14, 4.74) * mm, "end": v(2.8, 5.53) * mm});
            skSolve(sketch);
        }
        {
            var Q0;
            {var subQ0=sQuery(id+"F11.wireOp",EDGE,"E17");Q0=makeQuery(id+"F11.imprint","IMPRINT",FACE,{"disambiguationData":[TD([[makeQuery(id+"F11.imprint","IMPRINT",EDGE,{"derivedFrom":subQ0}),1.0]])]});}
            var Q1;
            {var subQ0=sQuery(id+"F11.wireOp",EDGE,"E16");Q1=makeQuery(id+"F11.imprint","IMPRINT",FACE,{"disambiguationData":[TD([[makeQuery(id+"F11.imprint","IMPRINT",EDGE,{"derivedFrom":subQ0}),1.0]])]});}
            var Q2;
            {var subQ0=sQuery(id+"F11.wireOp",EDGE,"E19");Q2=makeQuery(id+"F11.imprint","IMPRINT",FACE,{"disambiguationData":[TD([[makeQuery(id+"F11.imprint","IMPRINT",EDGE,{"derivedFrom":subQ0}),-1.0]])]});}
            var Q3;
            {var subQ0=sQuery(id+"F11.wireOp",EDGE,"E18");Q3=makeQuery(id+"F11.imprint","IMPRINT",FACE,{"disambiguationData":[TD([[makeQuery(id+"F11.imprint","IMPRINT",EDGE,{"derivedFrom":subQ0}),-1.0]])]});}
            var Q4;
            {var subQ0=sQuery(id+"F11.wireOp",EDGE,"E20.22.1");Q4=makeQuery(id+"F11.imprint","IMPRINT",FACE,{"disambiguationData":[TD([[makeQuery(id+"F11.imprint","IMPRINT",EDGE,{"derivedFrom":subQ0}),1.0]])]});}
            var Q5;
            {var subQ0=sQuery(id+"F11.wireOp",EDGE,"E20.22.2");Q5=makeQuery(id+"F11.imprint","IMPRINT",FACE,{"disambiguationData":[TD([[makeQuery(id+"F11.imprint","IMPRINT",EDGE,{"derivedFrom":subQ0}),1.0]])]});}
            var Q6;
            {var subQ0=sQuery(id+"F11.wireOp",EDGE,"E20.21.1");Q6=makeQuery(id+"F11.imprint","IMPRINT",FACE,{"disambiguationData":[TD([[makeQuery(id+"F11.imprint","IMPRINT",EDGE,{"derivedFrom":subQ0}),1.0]])]});}
            var Q7;
            {var subQ0=sQuery(id+"F11.wireOp",EDGE,"E20.21.2");Q7=makeQuery(id+"F11.imprint","IMPRINT",FACE,{"disambiguationData":[TD([[makeQuery(id+"F11.imprint","IMPRINT",EDGE,{"derivedFrom":subQ0}),1.0]])]});}
            var Q8;
            {var subQ0=sQuery(id+"F11.wireOp",EDGE,"E20.20.1");Q8=makeQuery(id+"F11.imprint","IMPRINT",FACE,{"disambiguationData":[TD([[makeQuery(id+"F11.imprint","IMPRINT",EDGE,{"derivedFrom":subQ0}),1.0]])]});}
            var Q9;
            {var subQ0=sQuery(id+"F11.wireOp",EDGE,"E20.20.2");Q9=makeQuery(id+"F11.imprint","IMPRINT",FACE,{"disambiguationData":[TD([[makeQuery(id+"F11.imprint","IMPRINT",EDGE,{"derivedFrom":subQ0}),1.0]])]});}
            var Q10;
            {var subQ0=sQuery(id+"F11.wireOp",EDGE,"E20.19.1");Q10=makeQuery(id+"F11.imprint","IMPRINT",FACE,{"disambiguationData":[TD([[makeQuery(id+"F11.imprint","IMPRINT",EDGE,{"derivedFrom":subQ0}),1.0]])]});}
            var Q11;
            {var subQ0=sQuery(id+"F11.wireOp",EDGE,"E20.19.2");Q11=makeQuery(id+"F11.imprint","IMPRINT",FACE,{"disambiguationData":[TD([[makeQuery(id+"F11.imprint","IMPRINT",EDGE,{"derivedFrom":subQ0}),1.0]])]});}
            var Q12;
            {var subQ0=sQuery(id+"F11.wireOp",EDGE,"E20.18.1");Q12=makeQuery(id+"F11.imprint","IMPRINT",FACE,{"disambiguationData":[TD([[makeQuery(id+"F11.imprint","IMPRINT",EDGE,{"derivedFrom":subQ0}),1.0]])]});}
            var Q13;
            {var subQ0=sQuery(id+"F11.wireOp",EDGE,"E20.18.2");Q13=makeQuery(id+"F11.imprint","IMPRINT",FACE,{"disambiguationData":[TD([[makeQuery(id+"F11.imprint","IMPRINT",EDGE,{"derivedFrom":subQ0}),1.0]])]});}
            var Q14;
            {var subQ0=sQuery(id+"F11.wireOp",EDGE,"E20.17.2");Q14=makeQuery(id+"F11.imprint","IMPRINT",FACE,{"disambiguationData":[TD([[makeQuery(id+"F11.imprint","IMPRINT",EDGE,{"derivedFrom":subQ0}),1.0]])]});}
            var Q15;
            {var subQ0=sQuery(id+"F11.wireOp",EDGE,"E20.17.1");Q15=makeQuery(id+"F11.imprint","IMPRINT",FACE,{"disambiguationData":[TD([[makeQuery(id+"F11.imprint","IMPRINT",EDGE,{"derivedFrom":subQ0}),1.0]])]});}
            var Q16;
            {var subQ0=sQuery(id+"F11.wireOp",EDGE,"E20.16.2");Q16=makeQuery(id+"F11.imprint","IMPRINT",FACE,{"disambiguationData":[TD([[makeQuery(id+"F11.imprint","IMPRINT",EDGE,{"derivedFrom":subQ0}),1.0]])]});}
            var Q17;
            {var subQ0=sQuery(id+"F11.wireOp",EDGE,"E20.16.1");Q17=makeQuery(id+"F11.imprint","IMPRINT",FACE,{"disambiguationData":[TD([[makeQuery(id+"F11.imprint","IMPRINT",EDGE,{"derivedFrom":subQ0}),1.0]])]});}
            var Q18;
            {var subQ0=sQuery(id+"F11.wireOp",EDGE,"E20.15.2");Q18=makeQuery(id+"F11.imprint","IMPRINT",FACE,{"disambiguationData":[TD([[makeQuery(id+"F11.imprint","IMPRINT",EDGE,{"derivedFrom":subQ0}),1.0]])]});}
            var Q19;
            {var subQ0=sQuery(id+"F11.wireOp",EDGE,"E20.15.1");Q19=makeQuery(id+"F11.imprint","IMPRINT",FACE,{"disambiguationData":[TD([[makeQuery(id+"F11.imprint","IMPRINT",EDGE,{"derivedFrom":subQ0}),1.0]])]});}
            var Q20;
            {var subQ0=sQuery(id+"F11.wireOp",EDGE,"E20.14.2");Q20=makeQuery(id+"F11.imprint","IMPRINT",FACE,{"disambiguationData":[TD([[makeQuery(id+"F11.imprint","IMPRINT",EDGE,{"derivedFrom":subQ0}),1.0]])]});}
            var Q21;
            {var subQ0=sQuery(id+"F11.wireOp",EDGE,"E20.14.1");Q21=makeQuery(id+"F11.imprint","IMPRINT",FACE,{"disambiguationData":[TD([[makeQuery(id+"F11.imprint","IMPRINT",EDGE,{"derivedFrom":subQ0}),1.0]])]});}
            var Q22;
            {var subQ0=sQuery(id+"F11.wireOp",EDGE,"E20.13.2");Q22=makeQuery(id+"F11.imprint","IMPRINT",FACE,{"disambiguationData":[TD([[makeQuery(id+"F11.imprint","IMPRINT",EDGE,{"derivedFrom":subQ0}),1.0]])]});}
            var Q23;
            {var subQ0=sQuery(id+"F11.wireOp",EDGE,"E20.13.1");Q23=makeQuery(id+"F11.imprint","IMPRINT",FACE,{"disambiguationData":[TD([[makeQuery(id+"F11.imprint","IMPRINT",EDGE,{"derivedFrom":subQ0}),1.0]])]});}
            var Q24;
            {var subQ0=sQuery(id+"F11.wireOp",EDGE,"E20.12.2");Q24=makeQuery(id+"F11.imprint","IMPRINT",FACE,{"disambiguationData":[TD([[makeQuery(id+"F11.imprint","IMPRINT",EDGE,{"derivedFrom":subQ0}),1.0]])]});}
            var Q25;
            {var subQ0=sQuery(id+"F11.wireOp",EDGE,"E20.12.1");Q25=makeQuery(id+"F11.imprint","IMPRINT",FACE,{"disambiguationData":[TD([[makeQuery(id+"F11.imprint","IMPRINT",EDGE,{"derivedFrom":subQ0}),1.0]])]});}
            var Q26;
            {var subQ0=sQuery(id+"F11.wireOp",EDGE,"E20.11.2");Q26=makeQuery(id+"F11.imprint","IMPRINT",FACE,{"disambiguationData":[TD([[makeQuery(id+"F11.imprint","IMPRINT",EDGE,{"derivedFrom":subQ0}),1.0]])]});}
            var Q27;
            {var subQ0=sQuery(id+"F11.wireOp",EDGE,"E20.11.1");Q27=makeQuery(id+"F11.imprint","IMPRINT",FACE,{"disambiguationData":[TD([[makeQuery(id+"F11.imprint","IMPRINT",EDGE,{"derivedFrom":subQ0}),1.0]])]});}
            var Q28;
            {var subQ0=sQuery(id+"F11.wireOp",EDGE,"E20.10.2");Q28=makeQuery(id+"F11.imprint","IMPRINT",FACE,{"disambiguationData":[TD([[makeQuery(id+"F11.imprint","IMPRINT",EDGE,{"derivedFrom":subQ0}),1.0]])]});}
            var Q29;
            {var subQ0=sQuery(id+"F11.wireOp",EDGE,"E20.10.1");Q29=makeQuery(id+"F11.imprint","IMPRINT",FACE,{"disambiguationData":[TD([[makeQuery(id+"F11.imprint","IMPRINT",EDGE,{"derivedFrom":subQ0}),1.0]])]});}
            var Q30;
            {var subQ0=sQuery(id+"F11.wireOp",EDGE,"E20.9.2");Q30=makeQuery(id+"F11.imprint","IMPRINT",FACE,{"disambiguationData":[TD([[makeQuery(id+"F11.imprint","IMPRINT",EDGE,{"derivedFrom":subQ0}),1.0]])]});}
            var Q31;
            {var subQ0=sQuery(id+"F11.wireOp",EDGE,"E20.9.1");Q31=makeQuery(id+"F11.imprint","IMPRINT",FACE,{"disambiguationData":[TD([[makeQuery(id+"F11.imprint","IMPRINT",EDGE,{"derivedFrom":subQ0}),1.0]])]});}
            var Q32;
            {var subQ0=sQuery(id+"F11.wireOp",EDGE,"E20.8.2");Q32=makeQuery(id+"F11.imprint","IMPRINT",FACE,{"disambiguationData":[TD([[makeQuery(id+"F11.imprint","IMPRINT",EDGE,{"derivedFrom":subQ0}),1.0]])]});}
            var Q33;
            {var subQ0=sQuery(id+"F11.wireOp",EDGE,"E20.8.1");Q33=makeQuery(id+"F11.imprint","IMPRINT",FACE,{"disambiguationData":[TD([[makeQuery(id+"F11.imprint","IMPRINT",EDGE,{"derivedFrom":subQ0}),1.0]])]});}
            var Q34;
            {var subQ0=sQuery(id+"F11.wireOp",EDGE,"E20.7.2");Q34=makeQuery(id+"F11.imprint","IMPRINT",FACE,{"disambiguationData":[TD([[makeQuery(id+"F11.imprint","IMPRINT",EDGE,{"derivedFrom":subQ0}),1.0]])]});}
            var Q35;
            {var subQ0=sQuery(id+"F11.wireOp",EDGE,"E20.7.1");Q35=makeQuery(id+"F11.imprint","IMPRINT",FACE,{"disambiguationData":[TD([[makeQuery(id+"F11.imprint","IMPRINT",EDGE,{"derivedFrom":subQ0}),1.0]])]});}
            var Q36;
            {var subQ0=sQuery(id+"F11.wireOp",EDGE,"E20.6.1");Q36=makeQuery(id+"F11.imprint","IMPRINT",FACE,{"disambiguationData":[TD([[makeQuery(id+"F11.imprint","IMPRINT",EDGE,{"derivedFrom":subQ0}),1.0]])]});}
            var Q37;
            {var subQ0=sQuery(id+"F11.wireOp",EDGE,"E20.6.2");Q37=makeQuery(id+"F11.imprint","IMPRINT",FACE,{"disambiguationData":[TD([[makeQuery(id+"F11.imprint","IMPRINT",EDGE,{"derivedFrom":subQ0}),1.0]])]});}
            var Q38;
            {var subQ0=sQuery(id+"F11.wireOp",EDGE,"E20.5.1");Q38=makeQuery(id+"F11.imprint","IMPRINT",FACE,{"disambiguationData":[TD([[makeQuery(id+"F11.imprint","IMPRINT",EDGE,{"derivedFrom":subQ0}),1.0]])]});}
            var Q39;
            {var subQ0=sQuery(id+"F11.wireOp",EDGE,"E20.5.2");Q39=makeQuery(id+"F11.imprint","IMPRINT",FACE,{"disambiguationData":[TD([[makeQuery(id+"F11.imprint","IMPRINT",EDGE,{"derivedFrom":subQ0}),1.0]])]});}
            var Q40;
            {var subQ0=sQuery(id+"F11.wireOp",EDGE,"E20.4.1");Q40=makeQuery(id+"F11.imprint","IMPRINT",FACE,{"disambiguationData":[TD([[makeQuery(id+"F11.imprint","IMPRINT",EDGE,{"derivedFrom":subQ0}),1.0]])]});}
            var Q41;
            {var subQ0=sQuery(id+"F11.wireOp",EDGE,"E20.4.2");Q41=makeQuery(id+"F11.imprint","IMPRINT",FACE,{"disambiguationData":[TD([[makeQuery(id+"F11.imprint","IMPRINT",EDGE,{"derivedFrom":subQ0}),1.0]])]});}
            var Q42;
            {var subQ0=sQuery(id+"F11.wireOp",EDGE,"E20.3.1");Q42=makeQuery(id+"F11.imprint","IMPRINT",FACE,{"disambiguationData":[TD([[makeQuery(id+"F11.imprint","IMPRINT",EDGE,{"derivedFrom":subQ0}),1.0]])]});}
            var Q43;
            {var subQ0=sQuery(id+"F11.wireOp",EDGE,"E20.3.2");Q43=makeQuery(id+"F11.imprint","IMPRINT",FACE,{"disambiguationData":[TD([[makeQuery(id+"F11.imprint","IMPRINT",EDGE,{"derivedFrom":subQ0}),1.0]])]});}
            var Q44;
            {var subQ0=sQuery(id+"F11.wireOp",EDGE,"E20.2.1");Q44=makeQuery(id+"F11.imprint","IMPRINT",FACE,{"disambiguationData":[TD([[makeQuery(id+"F11.imprint","IMPRINT",EDGE,{"derivedFrom":subQ0}),1.0]])]});}
            var Q45;
            {var subQ0=sQuery(id+"F11.wireOp",EDGE,"E20.2.2");Q45=makeQuery(id+"F11.imprint","IMPRINT",FACE,{"disambiguationData":[TD([[makeQuery(id+"F11.imprint","IMPRINT",EDGE,{"derivedFrom":subQ0}),1.0]])]});}
            var Q46;
            {var subQ0=sQuery(id+"F11.wireOp",EDGE,"E20.1.1");Q46=makeQuery(id+"F11.imprint","IMPRINT",FACE,{"disambiguationData":[TD([[makeQuery(id+"F11.imprint","IMPRINT",EDGE,{"derivedFrom":subQ0}),1.0]])]});}
            var Q47;
            {var subQ0=sQuery(id+"F11.wireOp",EDGE,"E20.1.2");Q47=makeQuery(id+"F11.imprint","IMPRINT",FACE,{"disambiguationData":[TD([[makeQuery(id+"F11.imprint","IMPRINT",EDGE,{"derivedFrom":subQ0}),1.0]])]});}
            extrude(context, id + "F12", {"entities" : qUnion([Q0, Q1, Q2, Q3, Q4, Q5, Q6, Q7, Q8, Q9, Q10, Q11, Q12, Q13, Q14, Q15, Q16, Q17, Q18, Q19, Q20, Q21, Q22, Q23, Q24, Q25, Q26, Q27, Q28, Q29, Q30, Q31, Q32, Q33, Q34, Q35, Q36, Q37, Q38, Q39, Q40, Q41, Q42, Q43, Q44, Q45, Q46, Q47]), "operationType" : NewBodyOperationType.REMOVE, "endBound" : BoundingType.UP_TO_NEXT, "oppositeDirection" : true, "depth" : 25 * mm});
        }
    });
